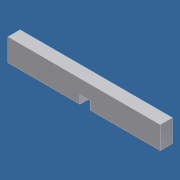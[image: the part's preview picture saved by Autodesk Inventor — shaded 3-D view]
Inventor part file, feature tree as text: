
AUTODESK INVENTOR PART (.ipt)
format: ipt  version: unknown  size: 166,912 bytes
history: native  units: in
note: dims shown in document units (in); Inventor stores cm internally (conversion verified against a paired STEP export)
features: extrude x1, sketch x1
ambient origin geometry x8: Origin, YZ Plane, XZ Plane, XY Plane, X Axis, Y Axis, Z Axis, Center Point
bodies: Solid1 (feature_tree)
feature tree (2):
  extrude  "Extrusion1"  Depth=2.312in
  sketch  "Sketch1"  dims[d0=0.3405in d1=2.312in d2=1.094in d5=0.125in d8=0.156in d9=0.1855in d10=0.0in]
